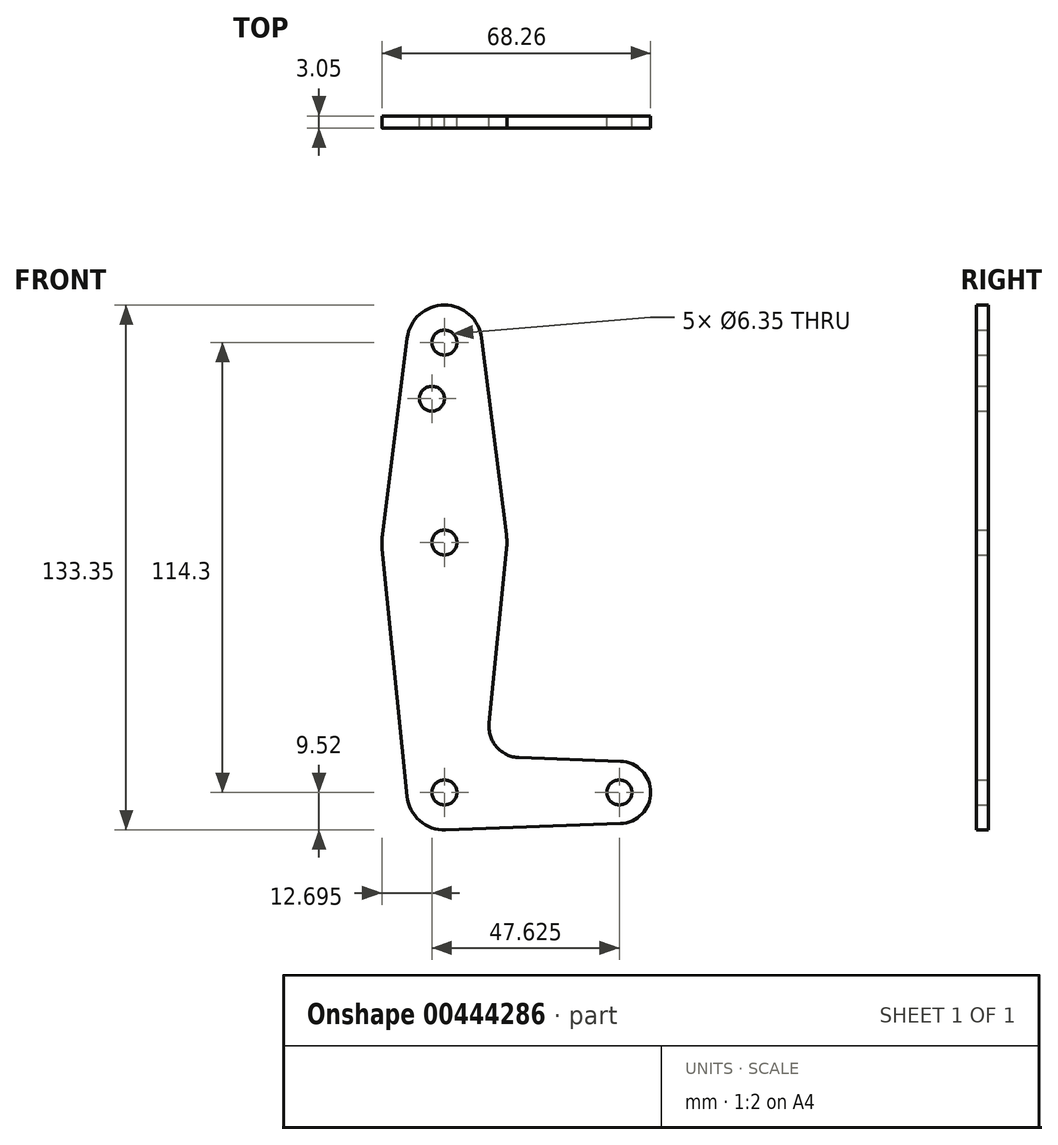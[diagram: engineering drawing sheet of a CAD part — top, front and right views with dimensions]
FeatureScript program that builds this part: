
annotation { "Feature Type Name" : "Feature", "Feature Type Description" : "" }
export const myFeature = defineFeature(function(context is Context, id is Id, definition is map)
    precondition{}
    {
        {
            var Q0;
            Q0=qCreatedBy(makeId("Front.planeOp"),FACE);
            var sketch = newSketch(context, id + "F0", { "sketchPlane" : qUnion([Q0])});
            skLineSegment(sketch, "E0", {"start": v(0, 0) * mm, "end": v(0, 114.3) * mm, "construction": true});
            skLineSegment(sketch, "E1", {"start": v(0, 0) * mm, "end": v(44.45, 0) * mm, "construction": true});
            skCircle(sketch, "E2", {"center": v(0, 114.3) * mm, "radius": 9.53 * mm});
            skCircle(sketch, "E3", {"center": v(0, 63.5) * mm, "radius": 15.88 * mm});
            skCircle(sketch, "E4", {"center": v(0, 0) * mm, "radius": 9.53 * mm});
            skCircle(sketch, "E5", {"center": v(44.45, 0) * mm, "radius": 7.94 * mm});
            skLineSegment(sketch, "E6", {"start": v(9.45, 115.5) * mm, "end": v(15.75, 65.48) * mm});
            skLineSegment(sketch, "E7", {"start": v(-9.45, 115.5) * mm, "end": v(-15.75, 65.48) * mm});
            skLineSegment(sketch, "E8", {"start": v(15.8, 61.91) * mm, "end": v(11.34, 17.6) * mm});
            skLineSegment(sketch, "E9", {"start": v(-9.48, -0.95) * mm, "end": v(-15.8, 61.91) * mm});
            skLineSegment(sketch, "E10", {"start": v(0.34, -9.52) * mm, "end": v(44.73, -7.93) * mm});
            skLineSegment(sketch, "E11", {"start": v(44.73, 7.93) * mm, "end": v(18.97, 8.85) * mm});
            skArc(sketch, "E12.filletArc", {"start": v(11.34, 17.6) * mm, "mid": v(13.26, 11.57) * mm, "end": v(18.97, 8.85) * mm});
            skCircle(sketch, "E13", {"center": v(0, 114.3) * mm, "radius": 3.18 * mm});
            skCircle(sketch, "E14", {"center": v(-3.18, 100.03) * mm, "radius": 3.18 * mm});
            skCircle(sketch, "E15", {"center": v(0, 63.5) * mm, "radius": 3.18 * mm});
            skCircle(sketch, "E16", {"center": v(0, 0) * mm, "radius": 3.18 * mm});
            skCircle(sketch, "E17", {"center": v(44.45, 0) * mm, "radius": 3.18 * mm});
            skSolve(sketch);
        }
        {
            var Q0;
            Q0 = qSketchRegion(id + "F0", true);
            extrude(context, id + "F1", {"entities" : qUnion([Q0]), "depth" : 3.05 * mm});
        }
    });
